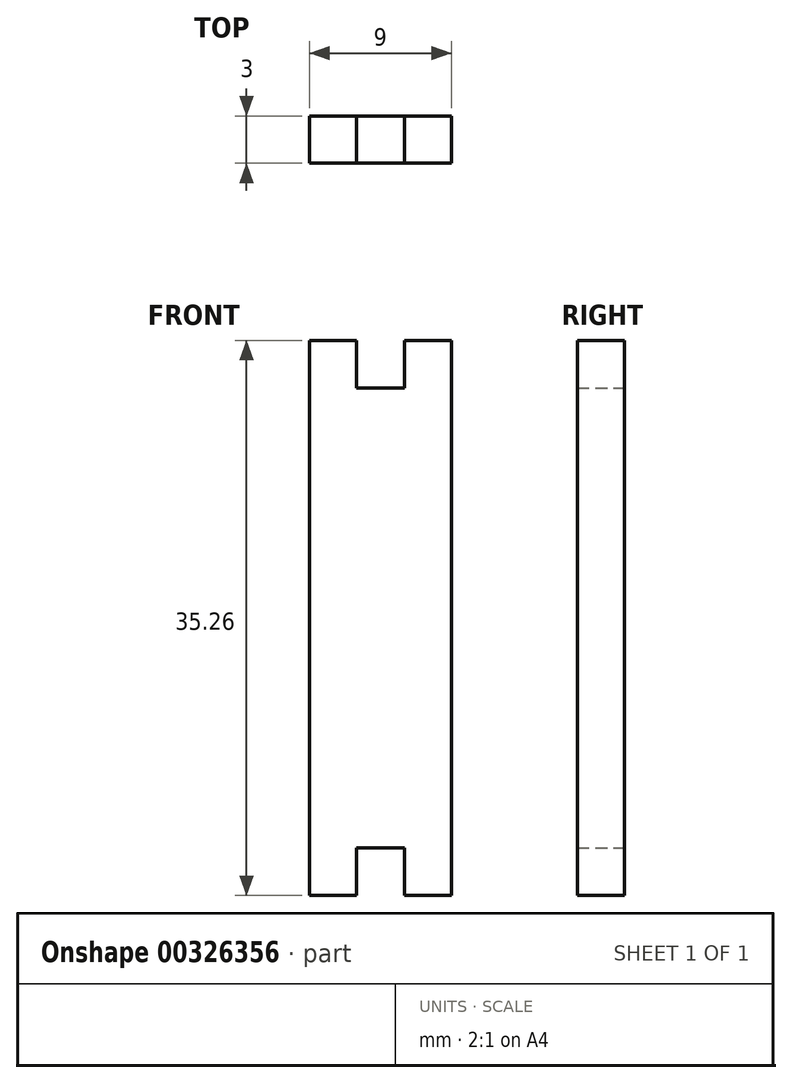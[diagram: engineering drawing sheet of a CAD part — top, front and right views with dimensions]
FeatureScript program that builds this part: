
annotation { "Feature Type Name" : "Feature", "Feature Type Description" : "" }
export const myFeature = defineFeature(function(context is Context, id is Id, definition is map)
    precondition{}
    {
        {
            var Q0;
            Q0=qCreatedBy(makeId("Front.planeOp"),FACE);
            var sketch = newSketch(context, id + "F0", { "sketchPlane" : qUnion([Q0])});
            skLineSegment(sketch, "E0", {"start": v(16.2, 19.96) * mm, "end": v(16.2, -15.3) * mm});
            skLineSegment(sketch, "E1", {"start": v(16.2, -15.3) * mm, "end": v(13.22, -15.3) * mm});
            skLineSegment(sketch, "E2", {"start": v(13.22, -15.3) * mm, "end": v(13.22, -12.28) * mm});
            skLineSegment(sketch, "E3", {"start": v(13.22, -12.28) * mm, "end": v(10.18, -12.28) * mm});
            skLineSegment(sketch, "E4", {"start": v(10.18, -12.28) * mm, "end": v(10.18, -15.3) * mm});
            skLineSegment(sketch, "E5", {"start": v(10.18, -15.3) * mm, "end": v(7.2, -15.3) * mm});
            skLineSegment(sketch, "E6", {"start": v(7.2, -15.3) * mm, "end": v(7.2, 19.96) * mm});
            skLineSegment(sketch, "E7", {"start": v(7.2, 19.96) * mm, "end": v(10.18, 19.96) * mm});
            skLineSegment(sketch, "E8", {"start": v(10.18, 19.96) * mm, "end": v(10.18, 16.94) * mm});
            skLineSegment(sketch, "E9", {"start": v(10.18, 16.94) * mm, "end": v(13.22, 16.94) * mm});
            skLineSegment(sketch, "E10", {"start": v(13.22, 16.94) * mm, "end": v(13.22, 19.96) * mm});
            skLineSegment(sketch, "E11", {"start": v(13.22, 19.96) * mm, "end": v(16.2, 19.96) * mm});
            skSolve(sketch);
        }
        {
            var Q0;
            Q0=makeQuery(id+"F0.imprint","IMPRINT",FACE,{"disambiguationData":[TD([[makeQuery(id+"F0.imprint","IMPRINT",EDGE,{"derivedFrom":sQuery(id+"F0.wireOp",EDGE,"E0")}),-1.0]])]});
            extrude(context, id + "F1", {"entities" : qUnion([Q0]), "depth" : 3 * mm});
        }
    });
